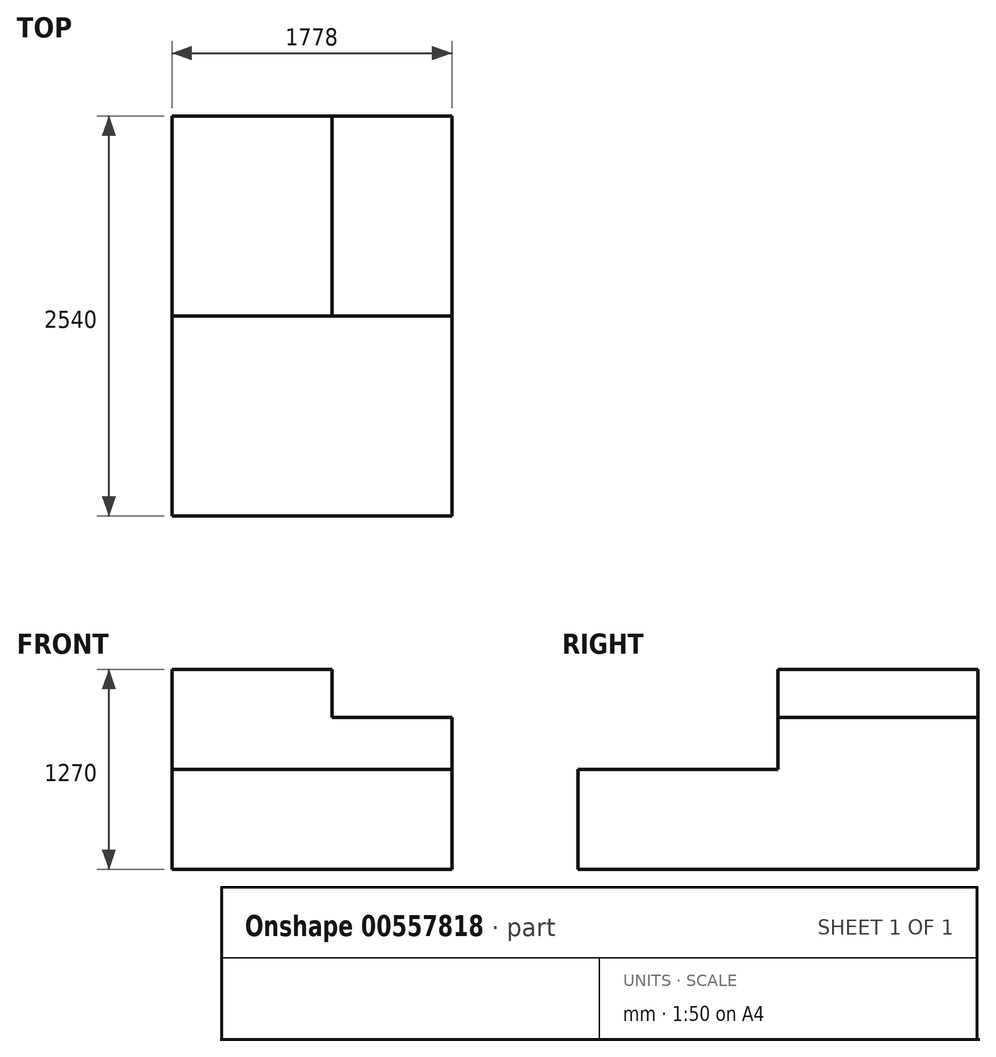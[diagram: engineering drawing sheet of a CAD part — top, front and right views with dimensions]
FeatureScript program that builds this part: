
annotation { "Feature Type Name" : "Feature", "Feature Type Description" : "" }
export const myFeature = defineFeature(function(context is Context, id is Id, definition is map)
    precondition{}
    {
        {
            var Q0;
            Q0=qCreatedBy(makeId("Right.planeOp"),FACE);
            var sketch = newSketch(context, id + "F0", { "sketchPlane" : qUnion([Q0])});
            skLineSegment(sketch, "E0", {"start": v(-81.93, -21.1) * mm, "end": v(2458.07, -21.1) * mm});
            skLineSegment(sketch, "E1", {"start": v(2458.07, -21.1) * mm, "end": v(2458.07, 944.1) * mm});
            skLineSegment(sketch, "E2", {"start": v(2458.07, 944.1) * mm, "end": v(1188.07, 944.1) * mm});
            skLineSegment(sketch, "E3", {"start": v(1188.07, 944.1) * mm, "end": v(1188.07, 613.9) * mm});
            skLineSegment(sketch, "E4", {"start": v(1188.07, 613.9) * mm, "end": v(-81.93, 613.9) * mm});
            skLineSegment(sketch, "E5", {"start": v(-81.93, 613.9) * mm, "end": v(-81.93, -21.1) * mm});
            skLineSegment(sketch, "E6", {"start": v(2458.07, 944.1) * mm, "end": v(2458.07, 1248.9) * mm});
            skLineSegment(sketch, "E7", {"start": v(2458.07, 1248.9) * mm, "end": v(1188.07, 1248.9) * mm});
            skLineSegment(sketch, "E8", {"start": v(1188.07, 1248.9) * mm, "end": v(1188.07, 944.1) * mm});
            skSolve(sketch);
        }
        {
            var Q0;
            Q0=makeQuery(id+"F0.imprint","IMPRINT",FACE,{"disambiguationData":[TD([[makeQuery(id+"F0.imprint","IMPRINT",EDGE,{"derivedFrom":sQuery(id+"F0.wireOp",EDGE,"E0")}),1.0]])]});
            extrude(context, id + "F1", {"entities" : qUnion([Q0]), "depth" : 1778 * mm, "offsetDistance" : 25.4 * mm});
        }
        {
            var Q0;
            Q0=makeQuery(id+"F0.imprint","IMPRINT",FACE,{"disambiguationData":[TD([[makeQuery(id+"F0.imprint","IMPRINT",EDGE,{"derivedFrom":sQuery(id+"F0.wireOp",EDGE,"E2")}),-1.0]])]});
            extrude(context, id + "F2", {"entities" : qUnion([Q0]), "operationType" : NewBodyOperationType.ADD, "depth" : 1016 * mm, "offsetDistance" : 25.4 * mm});
        }
    });
